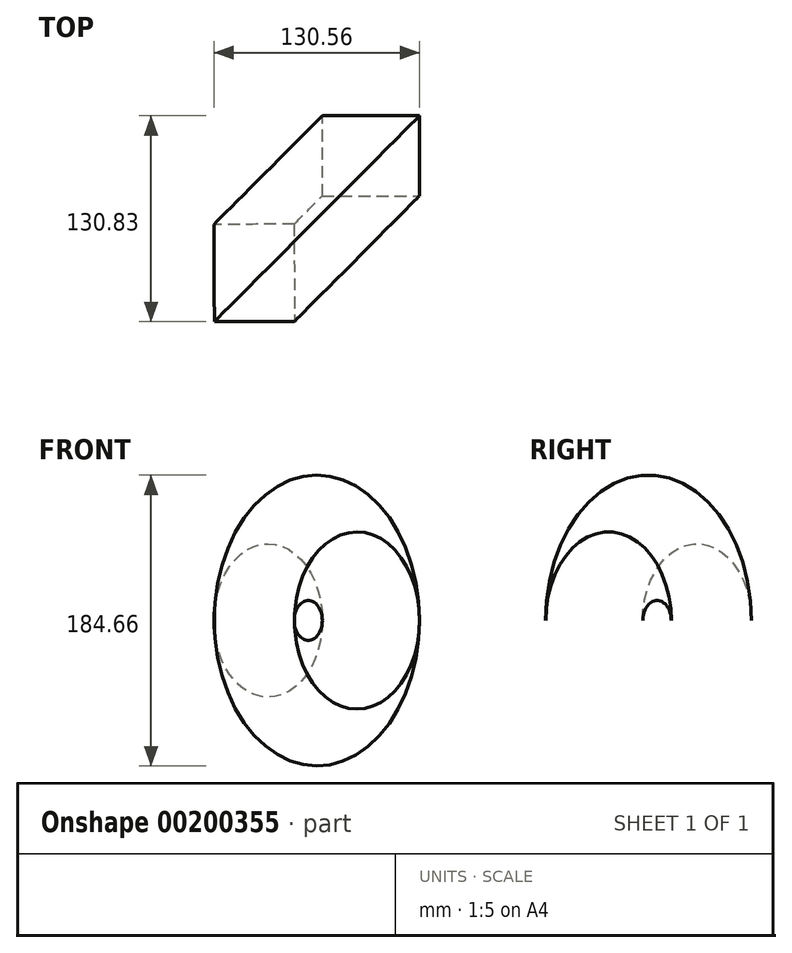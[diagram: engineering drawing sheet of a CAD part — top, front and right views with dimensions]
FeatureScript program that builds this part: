
annotation { "Feature Type Name" : "Feature", "Feature Type Description" : "" }
export const myFeature = defineFeature(function(context is Context, id is Id, definition is map)
    precondition{}
    {
        {
            var Q0;
            Q0=qCreatedBy(makeId("Top.planeOp"),FACE);
            var sketch = newSketch(context, id + "F0", { "sketchPlane" : qUnion([Q0])});
            skLineSegment(sketch, "E0.bottom", {"start": v(0, 0) * mm, "end": v(61.73, 0) * mm});
            skLineSegment(sketch, "E0.top", {"start": v(0, 50.9) * mm, "end": v(61.73, 50.9) * mm});
            skLineSegment(sketch, "E0.left", {"start": v(0, 0) * mm, "end": v(0, 50.9) * mm});
            skLineSegment(sketch, "E0.right", {"start": v(61.73, 0) * mm, "end": v(61.73, 50.9) * mm});
            skLineSegment(sketch, "E1", {"start": v(-69.6, 51.4) * mm, "end": v(55.82, -73.53) * mm});
            skSolve(sketch);
        }
        {
            var Q0;
            Q0=makeQuery(id+"F0.imprint","IMPRINT",FACE,{"disambiguationData":[TD([[makeQuery(id+"F0.imprint","IMPRINT",EDGE,{"derivedFrom":sQuery(id+"F0.wireOp",EDGE,"E0.bottom")}),1.0]])]});
            var Q1;
            Q1=sQuery(id+"F0.wireOp",EDGE,"E1");
            revolve(context, id + "F1", {"entities" : qUnion([Q0]), "axis" : qUnion([Q1]), "revolveType" : RevolveType.FULL});
        }
    });
